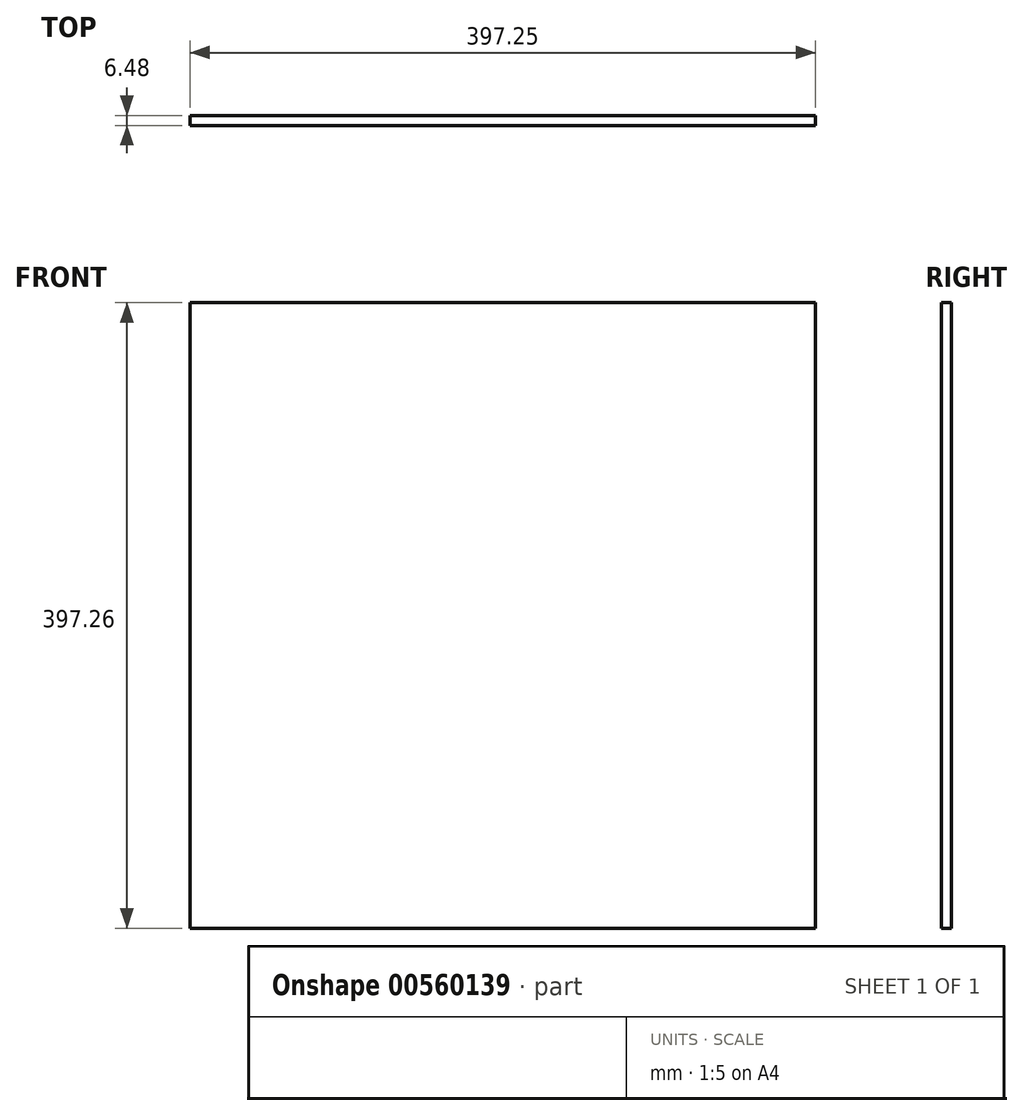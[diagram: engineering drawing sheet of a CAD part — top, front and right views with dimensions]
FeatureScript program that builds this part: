
annotation { "Feature Type Name" : "Feature", "Feature Type Description" : "" }
export const myFeature = defineFeature(function(context is Context, id is Id, definition is map)
    precondition{}
    {
        {
            var Q0;
            Q0=qCreatedBy(makeId("Front.planeOp"),FACE);
            var sketch = newSketch(context, id + "F0", { "sketchPlane" : qUnion([Q0])});
            skLineSegment(sketch, "E0.bottom", {"start": v(-261.72, 188.74) * mm, "end": v(135.53, 188.74) * mm});
            skLineSegment(sketch, "E0.top", {"start": v(-261.72, -208.52) * mm, "end": v(135.53, -208.52) * mm});
            skLineSegment(sketch, "E0.left", {"start": v(-261.72, 188.74) * mm, "end": v(-261.72, -208.52) * mm});
            skLineSegment(sketch, "E0.right", {"start": v(135.53, 188.74) * mm, "end": v(135.53, -208.52) * mm});
            skSolve(sketch);
        }
        {
            var Q0;
            Q0=makeQuery(id+"F0.imprint","IMPRINT",FACE,{"disambiguationData":[TD([[makeQuery(id+"F0.imprint","IMPRINT",EDGE,{"derivedFrom":sQuery(id+"F0.wireOp",EDGE,"E0.bottom")}),-1.0]])]});
            extrude(context, id + "F1", {"entities" : qUnion([Q0]), "depth" : 6.48 * mm, "offsetDistance" : 25.4 * mm});
        }
    });
